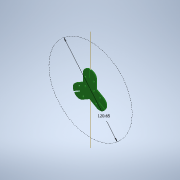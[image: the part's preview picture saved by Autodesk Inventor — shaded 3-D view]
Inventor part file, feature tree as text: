
AUTODESK INVENTOR PART (.ipt)
format: ipt  version: 2021 (Build 250183000, 183)  size: 141,824 bytes
history: native  units: in
note: dims shown in document units (in); Inventor stores cm internally (conversion verified against a paired STEP export)
features: imported_body x1, sketch x1, other x1
ambient origin geometry x8: Origin, YZ Plane, XZ Plane, XY Plane, X Axis, Y Axis, Z Axis, Center Point
bodies: Solid1 (feature_tree)
feature tree (3):
  imported_body  "Base1"
  sketch  "Sketch1"  dims[d0=4.75in]
  other  "Work Axis1"
